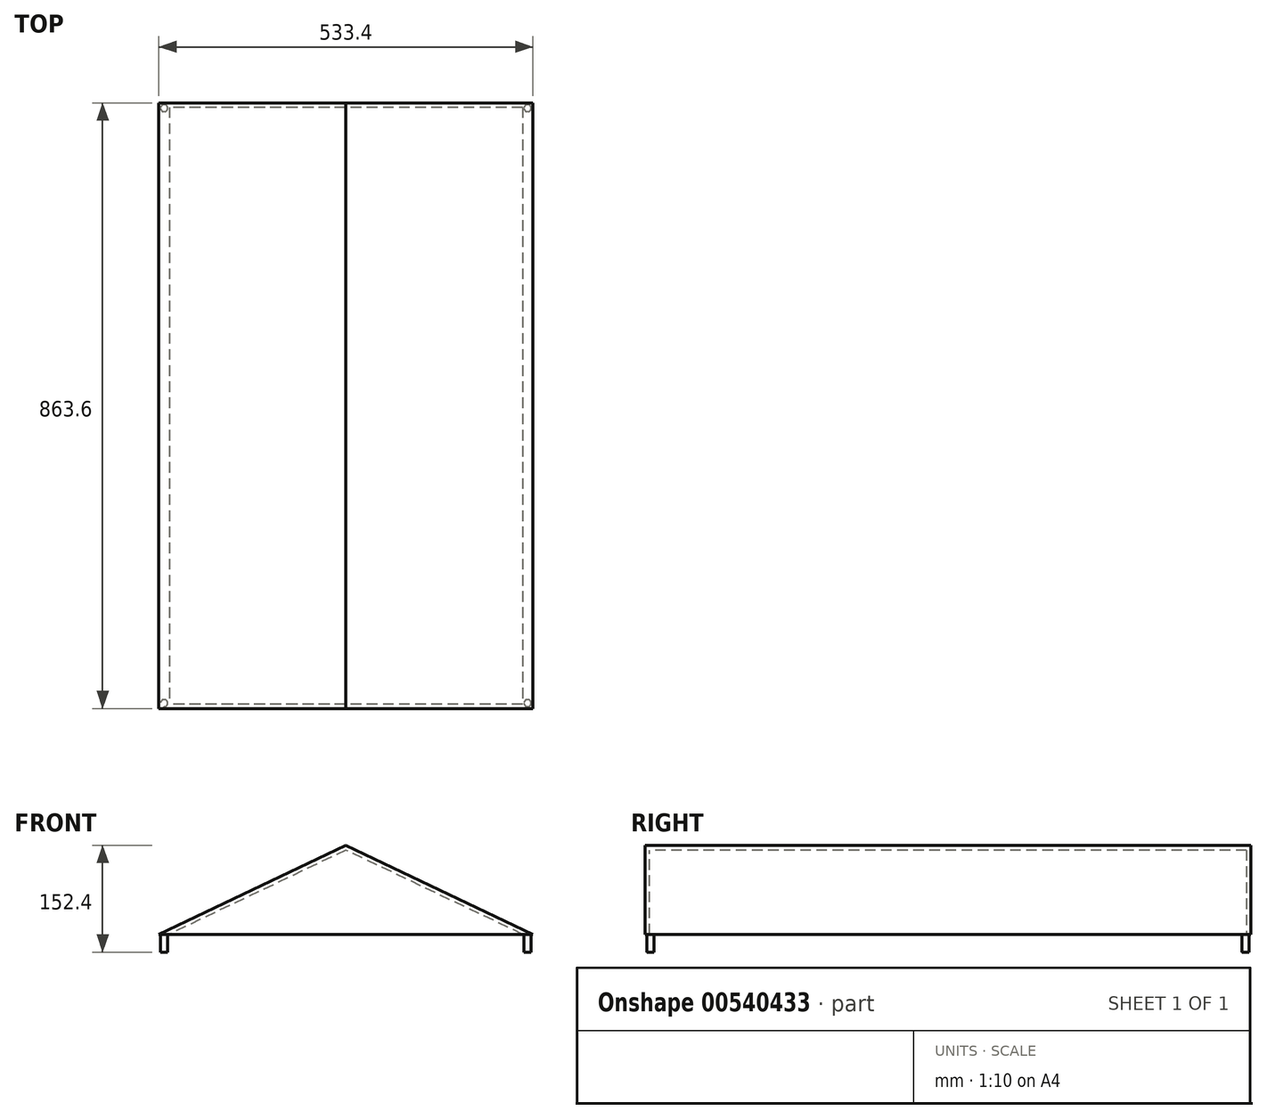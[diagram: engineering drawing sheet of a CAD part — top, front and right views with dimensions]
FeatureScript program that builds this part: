
annotation { "Feature Type Name" : "Feature", "Feature Type Description" : "" }
export const myFeature = defineFeature(function(context is Context, id is Id, definition is map)
    precondition{}
    {
        {
            var Q0;
            Q0=qCreatedBy(makeId("Top.planeOp"),FACE);
            var sketch = newSketch(context, id + "F0", { "sketchPlane" : qUnion([Q0])});
            skLineSegment(sketch, "E0.bottom", {"start": v(266.7, 431.8) * mm, "end": v(-266.7, 431.8) * mm});
            skLineSegment(sketch, "E0.top", {"start": v(266.7, -431.8) * mm, "end": v(-266.7, -431.8) * mm});
            skLineSegment(sketch, "E0.left", {"start": v(266.7, 431.8) * mm, "end": v(266.7, -431.8) * mm});
            skLineSegment(sketch, "E0.right", {"start": v(-266.7, 431.8) * mm, "end": v(-266.7, -431.8) * mm});
            skPoint(sketch, "E0.middle", {"position": v(0, 0) * mm});
            skSolve(sketch);
        }
        {
            var Q0;
            Q0=makeQuery(id+"F0.imprint","IMPRINT",FACE,{"disambiguationData":[TD([[makeQuery(id+"F0.imprint","IMPRINT",EDGE,{"derivedFrom":sQuery(id+"F0.wireOp",EDGE,"E0.bottom")}),1.0]])]});
            extrude(context, id + "F1", {"entities" : qUnion([Q0]), "depth" : 127 * mm, "offsetDistance" : 25.4 * mm});
        }
        {
            var Q0;
            Q0=makeQuery(id+"F1.opExtrude","SWEPT_FACE",FACE,{"disambiguationData":[OSD([sQuery(id+"F0.wireOp",EDGE,"E0.top")])]});
            var sketch = newSketch(context, id + "F2", { "sketchPlane" : qUnion([Q0])});
            skLineSegment(sketch, "E1", {"start": v(0, 127) * mm, "end": v(-266.7, 0) * mm});
            skLineSegment(sketch, "E2", {"start": v(-266.7, 0) * mm, "end": v(266.7, 0) * mm});
            skLineSegment(sketch, "E3", {"start": v(266.7, 0) * mm, "end": v(0, 127) * mm});
            skSolve(sketch);
        }
        {
            var Q0;
            {var subQ0=sQuery(id+"F2.wireOp",EDGE,"E1");Q0=makeQuery(id+"F2.imprint","IMPRINT",FACE,{"disambiguationData":[TD([[makeQuery(id+"F2.imprint","IMPRINT",EDGE,{"derivedFrom":subQ0}),-1.0]])]});}
            var Q1;
            {var subQ0=sQuery(id+"F2.wireOp",EDGE,"E3");Q1=makeQuery(id+"F2.imprint","IMPRINT",FACE,{"disambiguationData":[TD([[makeQuery(id+"F2.imprint","IMPRINT",EDGE,{"derivedFrom":subQ0}),-1.0]])]});}
            extrude(context, id + "F3", {"entities" : qUnion([Q0, Q1]), "operationType" : NewBodyOperationType.REMOVE, "oppositeDirection" : true, "depth" : 2540 * mm, "offsetDistance" : 25.4 * mm});
        }
        {
            var Q0;
            Q0=makeQuery(id+"F1.opExtrude","CAP_FACE",FACE,{"disambiguationData":[OSD([sQuery(id+"F0.wireOp",EDGE,"E0.bottom"),sQuery(id+"F0.wireOp",EDGE,"E0.top"),sQuery(id+"F0.wireOp",EDGE,"E0.left"),sQuery(id+"F0.wireOp",EDGE,"E0.right")])],"isStart":true});
            shell(context, id + "F4", {"entities" : qUnion([Q0]), "thickness" : 6.35 * mm});
        }
        {
            var Q0;
            Q0=makeQuery(id+"F1.opExtrude","CAP_FACE",FACE,{"disambiguationData":[OSD([sQuery(id+"F0.wireOp",EDGE,"E0.bottom"),sQuery(id+"F0.wireOp",EDGE,"E0.top"),sQuery(id+"F0.wireOp",EDGE,"E0.left"),sQuery(id+"F0.wireOp",EDGE,"E0.right")])],"isStart":true});
            var sketch = newSketch(context, id + "F5", { "sketchPlane" : qUnion([Q0])});
            skCircle(sketch, "E4", {"center": v(-259.08, 424.18) * mm, "radius": 5.08 * mm});
            skCircle(sketch, "E5", {"center": v(259.08, 424.18) * mm, "radius": 5.08 * mm});
            skCircle(sketch, "E6", {"center": v(259.08, -424.18) * mm, "radius": 5.08 * mm});
            skCircle(sketch, "E7", {"center": v(-259.08, -424.18) * mm, "radius": 5.08 * mm});
            skSolve(sketch);
        }
        {
            var Q0;
            Q0 = qSketchRegion(id + "F5", true);
            extrude(context, id + "F6", {"entities" : qUnion([Q0]), "operationType" : NewBodyOperationType.ADD, "depth" : 25.4 * mm, "offsetDistance" : 25.4 * mm});
        }
    });
